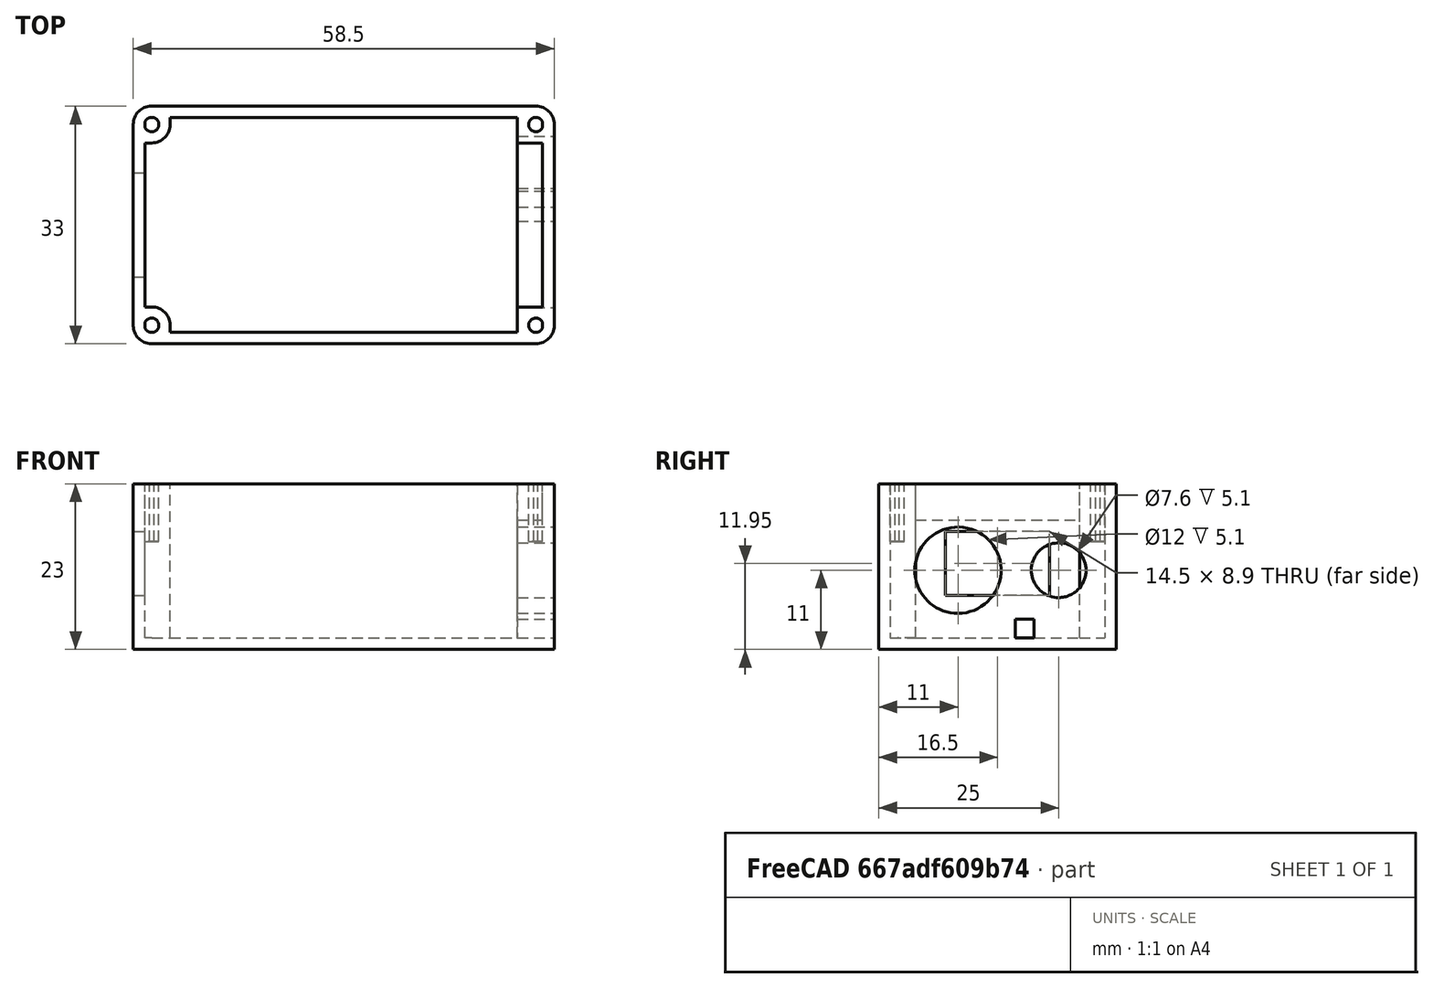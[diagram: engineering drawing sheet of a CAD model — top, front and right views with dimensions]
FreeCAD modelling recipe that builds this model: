
FCSTD DOCUMENT  (FreeCAD 0.16R)
Label: SolderungIronV2_ESD
License: All rights reserved
LicenseURL: http://en.wikipedia.org/wiki/All_rights_reserved
objects: Part::Box×9, Part::Cut×7, Part::Cylinder×6, Part::MultiFuse×4, Part::Fillet×1
note: 27 computed .brp shape members not serialized (recipe doc carries the construction recipe); baked Part::Feature solids carry a one-line shape summary decoded from their .brp

FEATURE [Part::Box] Box  label="Aussen"
  Height = 23
  Length = 58.5
  Width = 33
FEATURE [Part::Box] Box001  label="Innen"
  Height = 23
  Length = 55.3
  Placement = pos=(1.6,1.6,1.6) rot=(0,0,1;0rad)
  Width = 29.8
FEATURE [Part::Cut] Cut  label="Rohgehaeuse"
  Base = -> Box
  Tool = -> Box001
FEATURE [Part::Box] Box002  label="Schraubhalter"
  Height = 23
  Length = 5.1
  Width = 5.1
FEATURE [Part::Cylinder] Cylinder  label="Schraubloch"
  Angle = 360
  Height = 8
  Placement = pos=(2.55,2.55,15) rot=(0,0,1;0rad)
  Radius = 1
FEATURE [Part::Cut] Cut001  label="Platinenhalter000"
  Base = -> Box002
  Tool = -> Cylinder
FEATURE [Part::Box] Box003  label="Schraubhalter001"
  Height = 23
  Length = 5.1
  Width = 5.1
FEATURE [Part::Cylinder] Cylinder001  label="Schraubloch001"
  Angle = 360
  Height = 8
  Placement = pos=(2.55,2.55,15) rot=(0,0,1;0rad)
  Radius = 1
FEATURE [Part::Cut] Cut002  label="Platinenhalter001"
  Base = -> Box003
  Placement = pos=(53.4,0,0) rot=(0,0,1;0rad)
  Tool = -> Cylinder001
FEATURE [Part::Box] Box004  label="Schraubhalter002"
  Height = 23
  Length = 5.1
  Width = 5.1
FEATURE [Part::Cylinder] Cylinder002  label="Schraubloch002"
  Angle = 360
  Height = 8
  Placement = pos=(2.55,2.55,15) rot=(0,0,1;0rad)
  Radius = 1
FEATURE [Part::Cut] Cut003  label="Platinenhalter002"
  Base = -> Box004
  Placement = pos=(0,27.9,0) rot=(0,0,1;0rad)
  Tool = -> Cylinder002
FEATURE [Part::Box] Box005  label="Schraubhalter003"
  Height = 23
  Length = 5.1
  Width = 5.1
FEATURE [Part::Cylinder] Cylinder003  label="Schraubloch003"
  Angle = 360
  Height = 8
  Placement = pos=(2.55,2.55,15) rot=(0,0,1;0rad)
  Radius = 1
FEATURE [Part::Cut] Cut004  label="Platinenhalter003"
  Base = -> Box005
  Placement = pos=(53.4,27.9,0) rot=(0,0,1;0rad)
  Tool = -> Cylinder003
FEATURE [Part::MultiFuse] Fusion  label="Platinenhalter"
  Shapes = -> [Cut001,Cut002,Cut004,Cut003]
FEATURE [Part::MultiFuse] Fusion001  label="Grundgehaeuse"
  Shapes = -> [Cut,Fusion]
FEATURE [Part::Box] Box006  label="Switch"
  Height = 8.9
  Length = 10
  Placement = pos=(-3,9.25,7.5) rot=(0,0,1;0rad)
  Width = 14.5
FEATURE [Part::Cylinder] Cylinder004  label="Aviator"
  Angle = 360
  Height = 10
  Placement = pos=(50,11,11) rot=(0,1,0;1.5708rad)
  Radius = 6
FEATURE [Part::Cylinder] Cylinder005  label="DCPlug"
  Angle = 360
  Height = 10
  Placement = pos=(50,25,11) rot=(0,1,0;1.5708rad)
  Radius = 3.8
FEATURE [Part::Box] Box007  label="Lochverstaerkung"
  Height = 18
  Length = 5.1
  Placement = pos=(53.4,5.1,0) rot=(0,0,1;0rad)
  Width = 22.8
FEATURE [Part::MultiFuse] Fusion002  label="Gehaeusex"
  Shapes = -> [Fusion001,Box007]
FEATURE [Part::MultiFuse] Fusion003  label="Aussparungen"
  Shapes = -> [Box006,Cylinder004,Cylinder005]
FEATURE [Part::Fillet] Fillet  label="Gehaeusez"
  Base = -> Fusion002
  Edges = 6 edges r=2.5: [Edge1,Edge43,Edge45,Edge68,Edge95,Edge110]
FEATURE [Part::Cut] Cut005  label="Case_old"
  Base = -> Fillet
  Tool = -> Fusion003
FEATURE [Part::Box] Box008  label="Dupont"
  Height = 2.6
  Length = 10
  Placement = pos=(51,19,1.6) rot=(0,0,1;0rad)
  Width = 2.6
FEATURE [Part::Cut] Cut006  label="Case"
  Base = -> Cut005
  Tool = -> Box008
